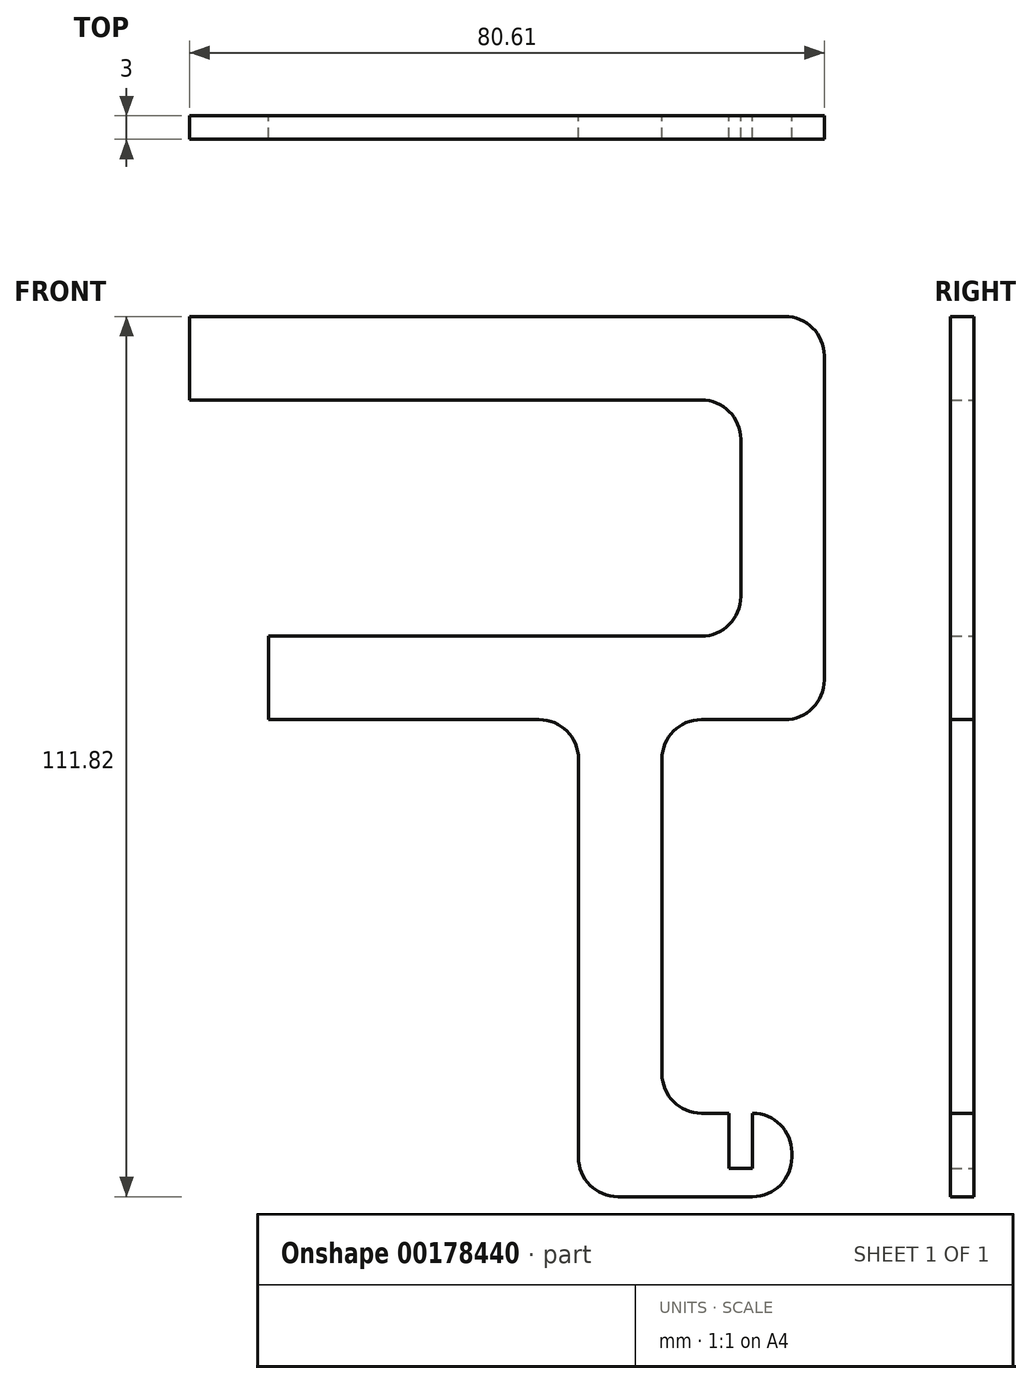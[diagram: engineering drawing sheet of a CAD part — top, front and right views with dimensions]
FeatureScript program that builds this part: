
annotation { "Feature Type Name" : "Feature", "Feature Type Description" : "" }
export const myFeature = defineFeature(function(context is Context, id is Id, definition is map)
    precondition{}
    {
        {
            var Q0;
            Q0=qCreatedBy(makeId("Front.planeOp"),FACE);
            var sketch = newSketch(context, id + "F0", { "sketchPlane" : qUnion([Q0])});
            skLineSegment(sketch, "E0.bottom", {"start": v(0, 0) * mm, "end": v(80.6, 0) * mm});
            skLineSegment(sketch, "E0.top", {"start": v(0, -10.6) * mm, "end": v(70, -10.6) * mm});
            skLineSegment(sketch, "E0.left", {"start": v(0, 0) * mm, "end": v(0, -10.6) * mm});
            skLineSegment(sketch, "E0.right", {"start": v(80.6, 0) * mm, "end": v(80.6, -51.21) * mm});
            skLineSegment(sketch, "E1.right", {"start": v(70, -10.6) * mm, "end": v(70, -40.6) * mm});
            skLineSegment(sketch, "E2.bottom", {"start": v(70, -40.6) * mm, "end": v(10, -40.6) * mm});
            skLineSegment(sketch, "E2.top", {"start": v(80.6, -51.21) * mm, "end": v(60, -51.21) * mm});
            skLineSegment(sketch, "E2.right", {"start": v(10, -40.6) * mm, "end": v(10, -51.21) * mm});
            skLineSegment(sketch, "E3.left", {"start": v(60, -51.21) * mm, "end": v(60, -101.21) * mm});
            skLineSegment(sketch, "E3.right", {"start": v(49.4, -51.21) * mm, "end": v(49.4, -111.82) * mm});
            skLineSegment(sketch, "E4.bottom", {"start": v(60, -101.21) * mm, "end": v(68.5, -101.21) * mm});
            skLineSegment(sketch, "E4.top", {"start": v(49.4, -111.82) * mm, "end": v(76.5, -111.82) * mm});
            skLineSegment(sketch, "E4.right", {"start": v(68.5, -101.21) * mm, "end": v(68.5, -108.21) * mm});
            skLineSegment(sketch, "E5.top", {"start": v(68.5, -108.21) * mm, "end": v(71.5, -108.21) * mm});
            skLineSegment(sketch, "E6.top", {"start": v(71.5, -101.21) * mm, "end": v(76.5, -101.21) * mm});
            skLineSegment(sketch, "E6.left", {"start": v(71.5, -108.21) * mm, "end": v(71.5, -101.21) * mm});
            skLineSegment(sketch, "E6.right", {"start": v(76.5, -111.82) * mm, "end": v(76.5, -101.21) * mm});
            skLineSegment(sketch, "E7.trimOffspring", {"start": v(49.4, -51.21) * mm, "end": v(10, -51.21) * mm});
            skLineSegment(sketch, "E8", {"start": v(70, -10.6) * mm, "end": v(80.6, 0) * mm, "construction": true});
            skLineSegment(sketch, "E9", {"start": v(70, -40.6) * mm, "end": v(80.6, -51.21) * mm, "construction": true});
            skLineSegment(sketch, "E10", {"start": v(60, -101.21) * mm, "end": v(49.4, -111.82) * mm, "construction": true});
            skPoint(sketch, "E11", {"position": v(70, -108.21) * mm});
            skSolve(sketch);
        }
        {
            var Q0;
            Q0 = qSketchRegion(id + "F0", true);
            extrude(context, id + "F1", {"entities" : qUnion([Q0]), "depth" : 3 * mm});
        }
        {
            var Q0;
            Q0=makeQuery(id+"F1.opExtrude","SWEPT_EDGE",EDGE,{"disambiguationData":[OSD([sQuery(id+"F0.wireOp",EDGE,"E3.right"),sQuery(id+"F0.wireOp",EDGE,"E7.trimOffspring")])]});
            var Q1;
            Q1=makeQuery(id+"F1.opExtrude","SWEPT_EDGE",EDGE,{"disambiguationData":[OSD([sQuery(id+"F0.wireOp",EDGE,"E0.top"),sQuery(id+"F0.wireOp",EDGE,"E1.right")])]});
            var Q2;
            Q2=makeQuery(id+"F1.opExtrude","SWEPT_EDGE",EDGE,{"disambiguationData":[OSD([sQuery(id+"F0.wireOp",EDGE,"E1.right"),sQuery(id+"F0.wireOp",EDGE,"E2.bottom")])]});
            var Q3;
            Q3=makeQuery(id+"F1.opExtrude","SWEPT_EDGE",EDGE,{"disambiguationData":[OSD([sQuery(id+"F0.wireOp",EDGE,"E0.bottom"),sQuery(id+"F0.wireOp",EDGE,"E0.right")])]});
            var Q4;
            Q4=makeQuery(id+"F1.opExtrude","SWEPT_EDGE",EDGE,{"disambiguationData":[OSD([sQuery(id+"F0.wireOp",EDGE,"E0.right"),sQuery(id+"F0.wireOp",EDGE,"E2.top")])]});
            var Q5;
            Q5=makeQuery(id+"F1.opExtrude","SWEPT_EDGE",EDGE,{"disambiguationData":[OSD([sQuery(id+"F0.wireOp",EDGE,"E2.top"),sQuery(id+"F0.wireOp",EDGE,"E3.left")])]});
            var Q6;
            Q6=makeQuery(id+"F1.opExtrude","SWEPT_EDGE",EDGE,{"disambiguationData":[OSD([sQuery(id+"F0.wireOp",EDGE,"E3.left"),sQuery(id+"F0.wireOp",EDGE,"E4.bottom")])]});
            var Q7;
            Q7=makeQuery(id+"F1.opExtrude","SWEPT_EDGE",EDGE,{"disambiguationData":[OSD([sQuery(id+"F0.wireOp",EDGE,"E6.top"),sQuery(id+"F0.wireOp",EDGE,"E6.right")])]});
            var Q8;
            Q8=makeQuery(id+"F1.opExtrude","SWEPT_EDGE",EDGE,{"disambiguationData":[OSD([sQuery(id+"F0.wireOp",EDGE,"E4.top"),sQuery(id+"F0.wireOp",EDGE,"E6.right")])]});
            var Q9;
            Q9=makeQuery(id+"F1.opExtrude","SWEPT_EDGE",EDGE,{"disambiguationData":[OSD([sQuery(id+"F0.wireOp",EDGE,"E3.right"),sQuery(id+"F0.wireOp",EDGE,"E4.top")])]});
            fillet(context, id + "F2", {"entities" : qUnion([Q0, Q1, Q2, Q3, Q4, Q5, Q6, Q7, Q8, Q9]), "radius" : 5 * mm, "tangentPropagation" : true, "allowEdgeOverflow" : false});
        }
    });
